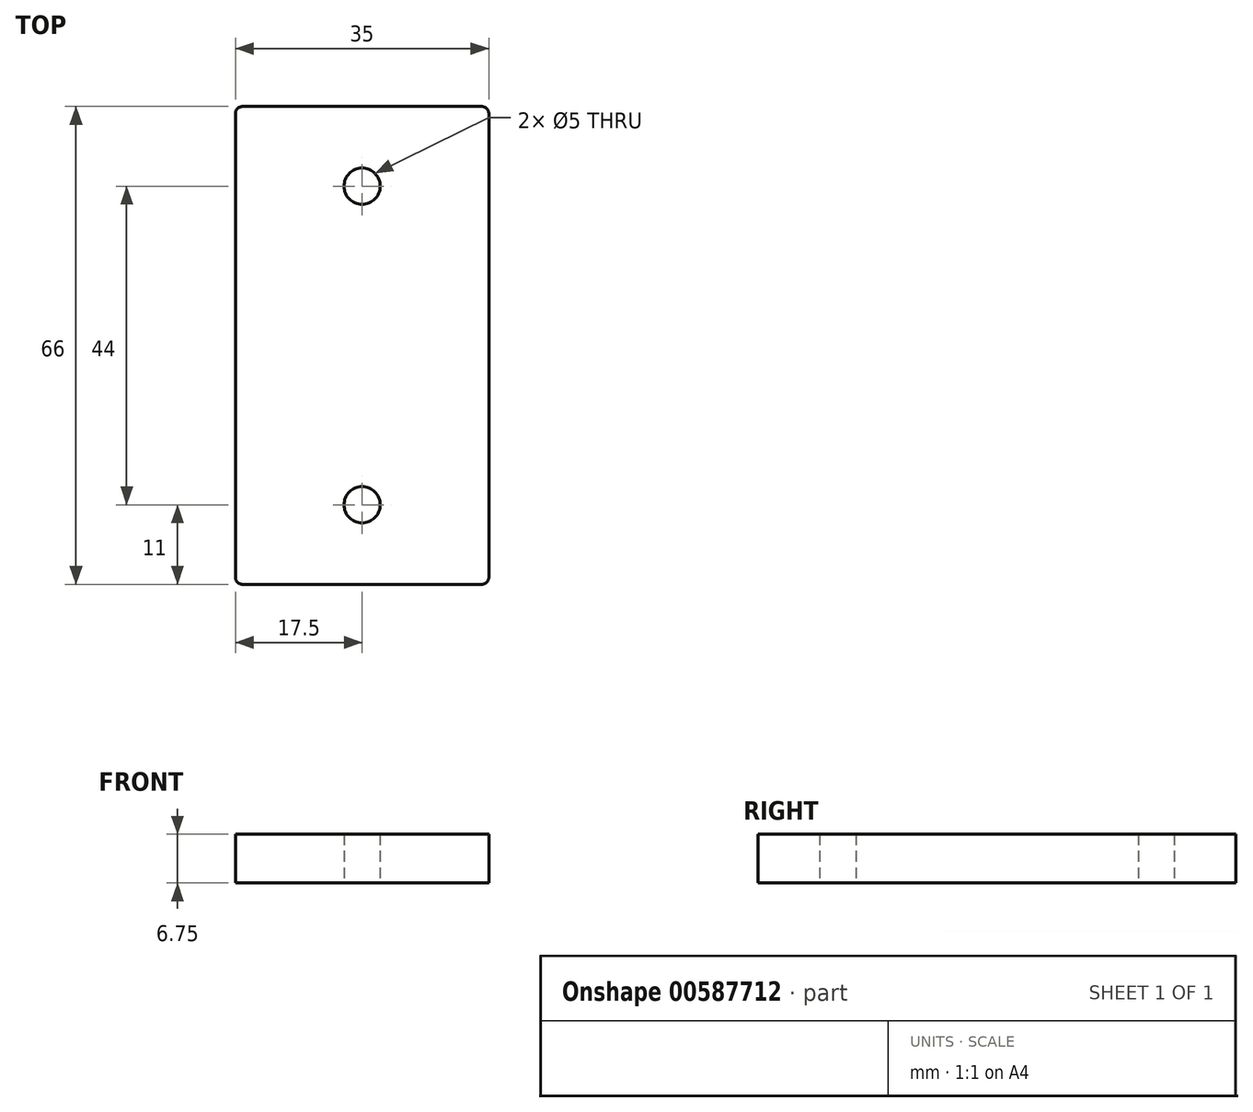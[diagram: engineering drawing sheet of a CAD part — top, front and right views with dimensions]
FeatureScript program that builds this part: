
annotation { "Feature Type Name" : "Feature", "Feature Type Description" : "" }
export const myFeature = defineFeature(function(context is Context, id is Id, definition is map)
    precondition{}
    {
        {
            var Q0;
            Q0=qCreatedBy(makeId("Top.planeOp"),FACE);
            var sketch = newSketch(context, id + "F0", { "sketchPlane" : qUnion([Q0])});
            skLineSegment(sketch, "E0.bottom", {"start": v(17.5, 33) * mm, "end": v(-17.5, 33) * mm});
            skLineSegment(sketch, "E0.top", {"start": v(17.5, -33) * mm, "end": v(-17.5, -33) * mm});
            skLineSegment(sketch, "E0.left", {"start": v(17.5, 33) * mm, "end": v(17.5, -33) * mm});
            skLineSegment(sketch, "E0.right", {"start": v(-17.5, 33) * mm, "end": v(-17.5, -33) * mm});
            skPoint(sketch, "E0.middle", {"position": v(0, 0) * mm});
            skCircle(sketch, "E1", {"center": v(0, 22) * mm, "radius": 2.5 * mm});
            skCircle(sketch, "E2", {"center": v(0, -22) * mm, "radius": 2.5 * mm});
            skSolve(sketch);
        }
        {
            var Q0;
            Q0 = qSketchRegion(id + "F0", true);
            extrude(context, id + "F1", {"entities" : qUnion([Q0]), "depth" : 6.75 * mm, "offsetDistance" : 25 * mm});
        }
        {
            var Q0;
            Q0=makeQuery(id+"F1.opExtrude","SWEPT_EDGE",EDGE,{"disambiguationData":[OSD([sQuery(id+"F0.wireOp",EDGE,"E0.bottom"),sQuery(id+"F0.wireOp",EDGE,"E0.right")])]});
            var Q1;
            Q1=makeQuery(id+"F1.opExtrude","SWEPT_EDGE",EDGE,{"disambiguationData":[OSD([sQuery(id+"F0.wireOp",EDGE,"E0.top"),sQuery(id+"F0.wireOp",EDGE,"E0.right")])]});
            var Q2;
            Q2=makeQuery(id+"F1.opExtrude","SWEPT_EDGE",EDGE,{"disambiguationData":[OSD([sQuery(id+"F0.wireOp",EDGE,"E0.top"),sQuery(id+"F0.wireOp",EDGE,"E0.left")])]});
            var Q3;
            Q3=makeQuery(id+"F1.opExtrude","SWEPT_EDGE",EDGE,{"disambiguationData":[OSD([sQuery(id+"F0.wireOp",EDGE,"E0.bottom"),sQuery(id+"F0.wireOp",EDGE,"E0.left")])]});
            fillet(context, id + "F2", {"entities" : qUnion([Q0, Q1, Q2, Q3]), "radius" : 1 * mm, "tangentPropagation" : true, "allowEdgeOverflow" : false});
        }
    });
